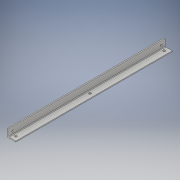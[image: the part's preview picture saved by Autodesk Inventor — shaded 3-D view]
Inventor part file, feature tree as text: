
AUTODESK INVENTOR PART (.ipt)
format: ipt  version: 2017 (Build 210142000, 142)  size: 128,512 bytes
history: native  units: in
note: dims shown in document units (in); Inventor stores cm internally (conversion verified against a paired STEP export)
features: sketch x4, hole x3, extrude x1
ambient origin geometry x8: Origin, YZ Plane, XZ Plane, XY Plane, X Axis, Y Axis, Z Axis, Center Point
bodies: Solid1 (feature_tree)
feature tree (8):
  extrude  "Extrusion1"  Depth=1.0in
  hole  "Hole1"  [1 undecoded]
  hole  "Hole2"  [1 undecoded]
  hole  "Hole3"  [1 undecoded]
  sketch  "Sketch1"  dims[d0=1.0in d1=1.0in]
  sketch  "Sketch2"  dims[d2=0.125in d3=19.375in d4=0.0in]
  sketch  "Sketch5"  dims[d5=0.5in d6=0.5in]
  sketch  "Sketch6"  dims[d7=0.7874in d9=18.375in d10=0.3937in d12=1.0in d14=0.281in d15=0.75in d16=0.385in d17=0.25in d18=0.5635in d19=1.0in d20=0.8108in d21=0.07in d24=0.281in d25=0.75in d26=0.385in d27=0.25in d28=0.5635in d29=1.0in d30=0.8108in d31=0.5in d32=0.5in d33=0.5in d34=18.375in d35=0.5in d36=0.281in d37=0.75in d38=0.385in d39=0.25in d40=0.5635in d41=1.0in d42=0.8108in]
note: 3 required parameter values undecoded (feature->parameter linkage not recoverable at this tier; creation-order binding heuristic only, values carry confidence <= 0.55)
